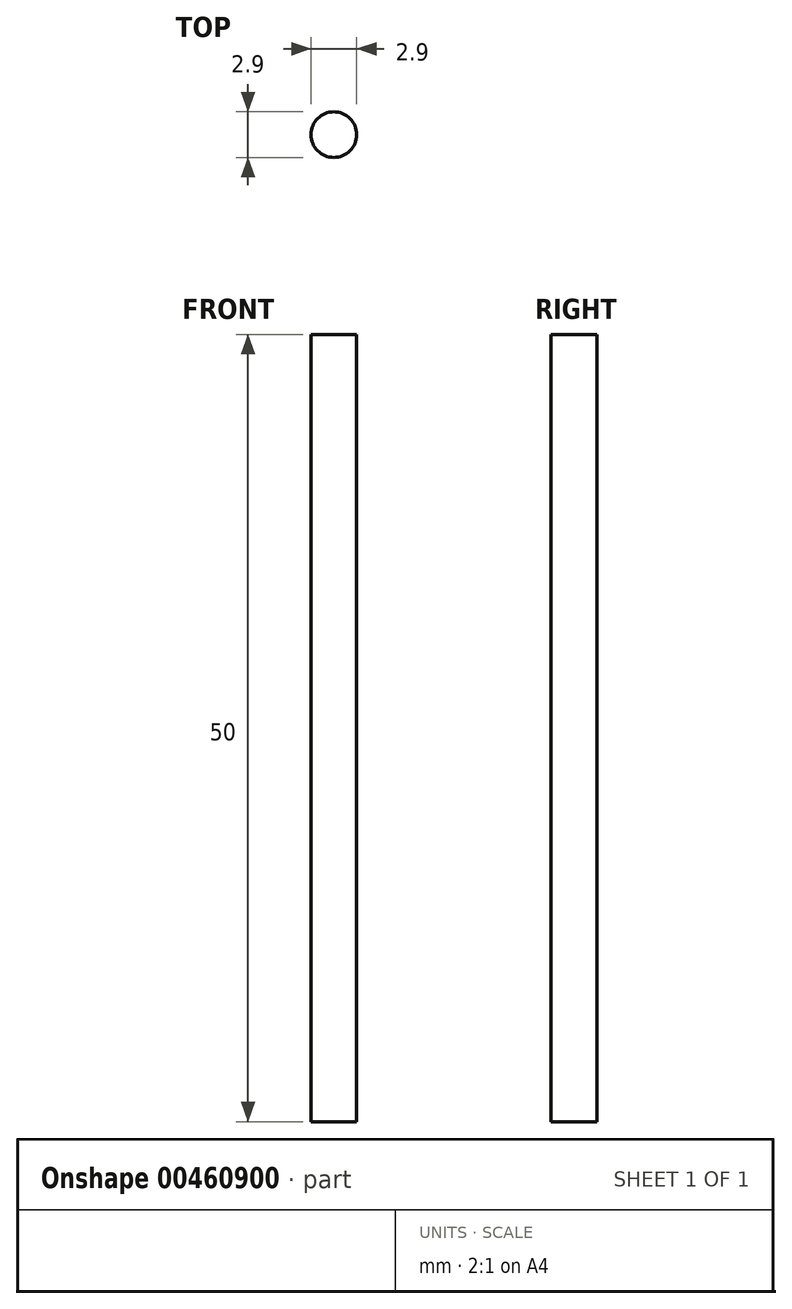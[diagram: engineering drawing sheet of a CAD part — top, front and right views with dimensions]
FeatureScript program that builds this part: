
annotation { "Feature Type Name" : "Feature", "Feature Type Description" : "" }
export const myFeature = defineFeature(function(context is Context, id is Id, definition is map)
    precondition{}
    {
        {
            var Q0;
            Q0=qCreatedBy(makeId("Top.planeOp"),FACE);
            var sketch = newSketch(context, id + "F0", { "sketchPlane" : qUnion([Q0])});
            skCircle(sketch, "E0", {"center": v(0, 0) * mm, "radius": 1.45 * mm});
            skSolve(sketch);
        }
        {
            var Q0;
            Q0=makeQuery(id+"F0.imprint","IMPRINT",FACE,{"disambiguationData":[TD([[makeQuery(id+"F0.imprint","IMPRINT",EDGE,{"derivedFrom":sQuery(id+"F0.wireOp",EDGE,"E0")}),1.0]])]});
            extrude(context, id + "F1", {"entities" : qUnion([Q0]), "depth" : 50 * mm});
        }
    });
